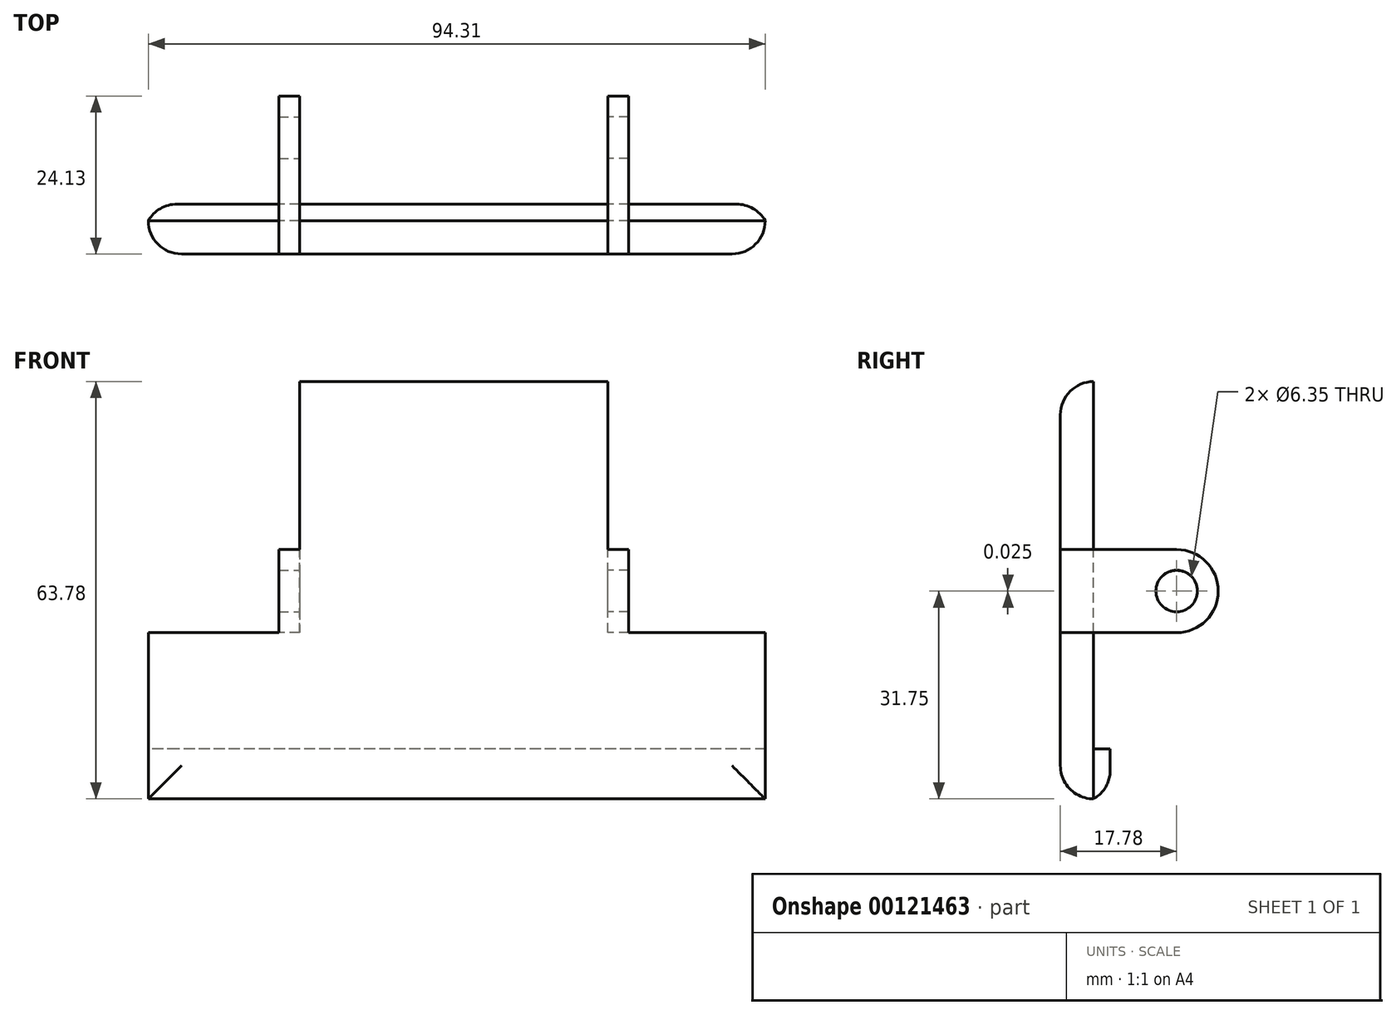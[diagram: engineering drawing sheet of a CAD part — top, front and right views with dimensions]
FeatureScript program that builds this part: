
annotation { "Feature Type Name" : "Feature", "Feature Type Description" : "" }
export const myFeature = defineFeature(function(context is Context, id is Id, definition is map)
    precondition{}
    {
        {
            var Q0;
            Q0=qCreatedBy(makeId("Front.planeOp"),FACE);
            var sketch = newSketch(context, id + "F0", { "sketchPlane" : qUnion([Q0])});
            skLineSegment(sketch, "E0", {"start": v(-23.12, 0) * mm, "end": v(-46.24, 0) * mm});
            skLineSegment(sketch, "E1", {"start": v(-46.24, 0) * mm, "end": v(-46.24, -25.4) * mm});
            skLineSegment(sketch, "E2", {"start": v(-46.24, -25.4) * mm, "end": v(48.07, -25.4) * mm});
            skLineSegment(sketch, "E3", {"start": v(48.07, -25.4) * mm, "end": v(48.07, 0) * mm});
            skLineSegment(sketch, "E4", {"start": v(48.07, 0) * mm, "end": v(24.03, 0) * mm});
            skLineSegment(sketch, "E5", {"start": v(-23.12, 0) * mm, "end": v(-23.12, 38.38) * mm});
            skLineSegment(sketch, "E6", {"start": v(24.03, 0) * mm, "end": v(24.03, 38.38) * mm});
            skLineSegment(sketch, "E7", {"start": v(24.03, 38.38) * mm, "end": v(-23.12, 38.38) * mm});
            skPoint(sketch, "E8.orphan", {"position": v(0, 0) * mm});
            skSolve(sketch);
        }
        {
            var Q0;
            Q0=makeQuery(id+"F0.imprint","IMPRINT",FACE,{"disambiguationData":[TD([[makeQuery(id+"F0.imprint","IMPRINT",EDGE,{"derivedFrom":sQuery(id+"F0.wireOp",EDGE,"E0")}),1.0]])]});
            extrude(context, id + "F1", {"entities" : qUnion([Q0]), "depth" : 5.08 * mm});
        }
        {
            var Q0;
            Q0=makeQuery(id+"F1.opExtrude","CAP_EDGE",EDGE,{"disambiguationData":[OSD([sQuery(id+"F0.wireOp",EDGE,"E1")])],"isStart":false});
            var Q1;
            Q1=makeQuery(id+"F1.opExtrude","CAP_EDGE",EDGE,{"disambiguationData":[OSD([sQuery(id+"F0.wireOp",EDGE,"E3")])],"isStart":false});
            var Q2;
            Q2=makeQuery(id+"F1.opExtrude","CAP_EDGE",EDGE,{"disambiguationData":[OSD([sQuery(id+"F0.wireOp",EDGE,"E2")])],"isStart":false});
            var Q3;
            Q3=makeQuery(id+"F1.opExtrude","CAP_EDGE",EDGE,{"disambiguationData":[OSD([sQuery(id+"F0.wireOp",EDGE,"E7")])],"isStart":false});
            fillet(context, id + "F2", {"entities" : qUnion([Q0, Q1, Q2, Q3]), "radius" : 5.08 * mm, "tangentPropagation" : true, "allowEdgeOverflow" : false});
        }
        {
            var Q0;
            Q0=makeQuery(id+"F1.opExtrude","SWEPT_FACE",FACE,{"disambiguationData":[OSD([sQuery(id+"F0.wireOp",EDGE,"E5")])]});
            var sketch = newSketch(context, id + "F3", { "sketchPlane" : qUnion([Q0])});
            skLineSegment(sketch, "E9", {"start": v(5.08, 0) * mm, "end": v(5.08, 12.7) * mm});
            skLineSegment(sketch, "E10", {"start": v(5.08, 12.7) * mm, "end": v(-12.7, 12.7) * mm});
            skLineSegment(sketch, "E11", {"start": v(-12.7, 0) * mm, "end": v(5.08, 0) * mm});
            skArc(sketch, "E12", {"start": v(-12.7, 12.7) * mm, "mid": v(-19.05, 6.35) * mm, "end": v(-12.7, 0) * mm});
            skCircle(sketch, "E13", {"center": v(-12.7, 6.35) * mm, "radius": 3.18 * mm});
            skSolve(sketch);
        }
        {
            var Q0;
            {var subQ3=sQuery(id+"F3.wireOp",EDGE,"E12");Q0=makeQuery(id+"F3.imprint","IMPRINT",FACE,{"disambiguationData":[TD([[makeQuery(id+"F3.imprint","IMPRINT",EDGE,{"derivedFrom":subQ3}),1.0]])]});}
            var Q1;
            {var subQ0=sQuery(id+"F3.wireOp",EDGE,"E9");Q1=makeQuery(id+"F3.imprint","IMPRINT",FACE,{"disambiguationData":[TD([[makeQuery(id+"F3.imprint","IMPRINT",EDGE,{"derivedFrom":subQ0}),1.0]])]});}
            extrude(context, id + "F4", {"entities" : qUnion([Q0, Q1]), "operationType" : NewBodyOperationType.ADD, "depth" : 3.17 * mm});
        }
        {
            var Q0;
            Q0=makeQuery(id+"F1.opExtrude","SWEPT_FACE",FACE,{"disambiguationData":[OSD([sQuery(id+"F0.wireOp",EDGE,"E6")])]});
            var sketch = newSketch(context, id + "F5", { "sketchPlane" : qUnion([Q0])});
            skLineSegment(sketch, "E14.bottom", {"start": v(-5.08, 0) * mm, "end": v(12.7, 0) * mm});
            skLineSegment(sketch, "E14.top", {"start": v(-5.08, 12.7) * mm, "end": v(12.7, 12.7) * mm});
            skLineSegment(sketch, "E14.left", {"start": v(-5.08, 0) * mm, "end": v(-5.08, 12.7) * mm});
            skCircle(sketch, "E15", {"center": v(12.7, 6.37) * mm, "radius": 3.18 * mm});
            skArc(sketch, "E16", {"start": v(12.7, 0) * mm, "mid": v(19.05, 6.35) * mm, "end": v(12.7, 12.7) * mm});
            skSolve(sketch);
        }
        {
            var Q0;
            Q0=makeQuery(id+"F5.imprint","IMPRINT",FACE,{"disambiguationData":[TD([[makeQuery(id+"F5.imprint","IMPRINT",EDGE,{"derivedFrom":sQuery(id+"F5.wireOp",EDGE,"E15")}),-1.0]])]});
            var Q1;
            {var subQ4=sQuery(id+"F5.wireOp",EDGE,"E14.left");Q1=makeQuery(id+"F5.imprint","IMPRINT",FACE,{"disambiguationData":[TD([[makeQuery(id+"F5.imprint","IMPRINT",EDGE,{"derivedFrom":subQ4}),-1.0]])]});}
            extrude(context, id + "F6", {"entities" : qUnion([Q0, Q1]), "operationType" : NewBodyOperationType.ADD, "depth" : 3.17 * mm});
        }
        {
            var Q0;
            Q0=makeQuery(id+"F1.opExtrude","CAP_FACE",FACE,{"disambiguationData":[OSD([sQuery(id+"F0.wireOp",EDGE,"E0"),sQuery(id+"F0.wireOp",EDGE,"E1"),sQuery(id+"F0.wireOp",EDGE,"E2"),sQuery(id+"F0.wireOp",EDGE,"E3"),sQuery(id+"F0.wireOp",EDGE,"E4"),sQuery(id+"F0.wireOp",EDGE,"E5"),sQuery(id+"F0.wireOp",EDGE,"E6"),sQuery(id+"F0.wireOp",EDGE,"E7")])],"isStart":true});
            var sketch = newSketch(context, id + "F7", { "sketchPlane" : qUnion([Q0])});
            skLineSegment(sketch, "E17.bottom", {"start": v(-48.07, -25.4) * mm, "end": v(46.24, -25.4) * mm});
            skLineSegment(sketch, "E17.top", {"start": v(-48.07, -17.78) * mm, "end": v(46.24, -17.78) * mm});
            skLineSegment(sketch, "E17.left", {"start": v(-48.07, -25.4) * mm, "end": v(-48.07, -17.78) * mm});
            skLineSegment(sketch, "E17.right", {"start": v(46.24, -25.4) * mm, "end": v(46.24, -17.78) * mm});
            skSolve(sketch);
        }
        {
            var Q0;
            Q0=makeQuery(id+"F7.imprint","IMPRINT",FACE,{"disambiguationData":[TD([[makeQuery(id+"F7.imprint","IMPRINT",EDGE,{"derivedFrom":sQuery(id+"F7.wireOp",EDGE,"E17.bottom")}),-1.0]])]});
            extrude(context, id + "F8", {"entities" : qUnion([Q0]), "operationType" : NewBodyOperationType.ADD, "depth" : 2.54 * mm});
        }
        {
            var Q0;
            Q0=makeQuery(id+"F8.opExtrude","CAP_EDGE",EDGE,{"disambiguationData":[OSD([sQuery(id+"F7.wireOp",EDGE,"E17.right")])],"isStart":false});
            var Q1;
            Q1=makeQuery(id+"F8.opExtrude","CAP_EDGE",EDGE,{"disambiguationData":[OSD([sQuery(id+"F7.wireOp",EDGE,"E17.bottom")])],"isStart":false});
            var Q2;
            Q2=makeQuery(id+"F8.opExtrude","CAP_EDGE",EDGE,{"disambiguationData":[OSD([sQuery(id+"F7.wireOp",EDGE,"E17.left")])],"isStart":false});
            fillet(context, id + "F9", {"entities" : qUnion([Q0, Q1, Q2]), "radius" : 5.08 * mm, "tangentPropagation" : true, "allowEdgeOverflow" : false});
        }
    });
